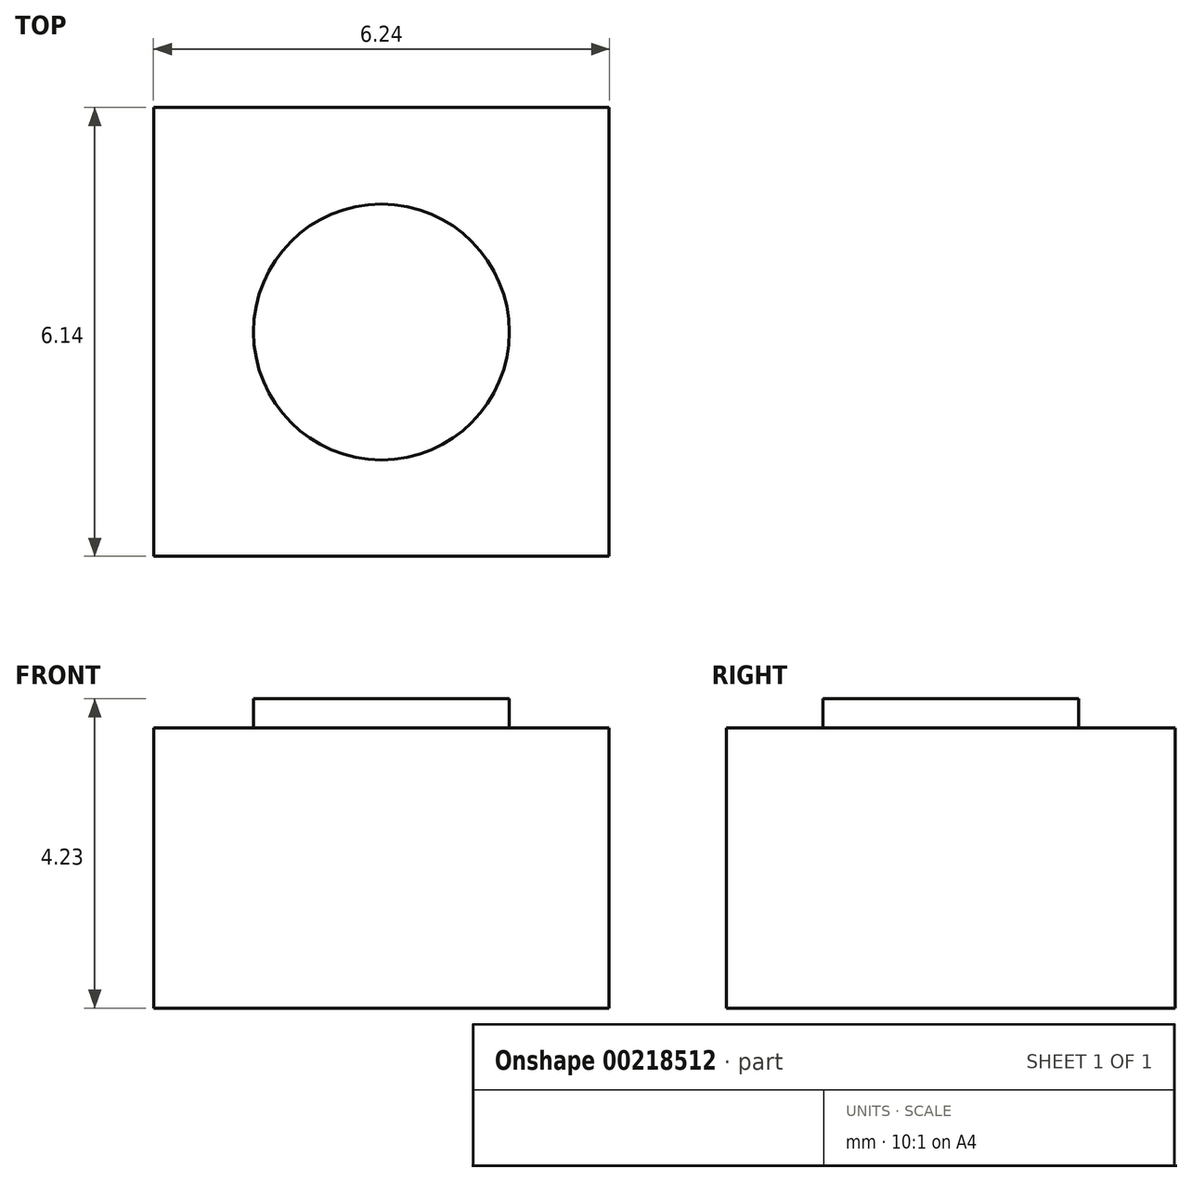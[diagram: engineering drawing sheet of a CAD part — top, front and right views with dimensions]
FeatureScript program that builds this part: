
annotation { "Feature Type Name" : "Feature", "Feature Type Description" : "" }
export const myFeature = defineFeature(function(context is Context, id is Id, definition is map)
    precondition{}
    {
        {
            var Q0;
            Q0=qCreatedBy(makeId("Top.planeOp"),FACE);
            var sketch = newSketch(context, id + "F0", { "sketchPlane" : qUnion([Q0])});
            skLineSegment(sketch, "E0.bottom", {"start": v(-3.12, 3.07) * mm, "end": v(3.12, 3.07) * mm});
            skLineSegment(sketch, "E0.top", {"start": v(-3.11, -3.07) * mm, "end": v(3.11, -3.07) * mm});
            skLineSegment(sketch, "E0.left", {"start": v(-3.11, 3.07) * mm, "end": v(-3.11, -3.07) * mm});
            skLineSegment(sketch, "E0.right", {"start": v(3.11, 3.07) * mm, "end": v(3.11, -3.07) * mm});
            skPoint(sketch, "E1", {"position": v(0, 3.07) * mm});
            skPoint(sketch, "E2", {"position": v(-3.11, 0) * mm});
            skSolve(sketch);
        }
        {
            var Q0;
            Q0 = qSketchRegion(id + "F0", true);
            var Q1;
            Q1=makeQuery(id+"F0.imprint","IMPRINT",FACE,{"disambiguationData":[TD([[makeQuery(id+"F0.imprint","IMPRINT",EDGE,{"derivedFrom":sQuery(id+"F0.wireOp",EDGE,"E0.bottom")}),-1.0]])]});
            extrude(context, id + "F1", {"entities" : qUnion([Q0, Q1]), "depth" : 3.83 * mm});
        }
        {
            var Q0;
            Q0=makeQuery(id+"F1.opExtrude","CAP_FACE",FACE,{"disambiguationData":[OSD([sQuery(id+"F0.wireOp",EDGE,"E0.bottom"),sQuery(id+"F0.wireOp",EDGE,"E0.top"),sQuery(id+"F0.wireOp",EDGE,"E0.left"),sQuery(id+"F0.wireOp",EDGE,"E0.right")])],"isStart":false});
            var sketch = newSketch(context, id + "F2", { "sketchPlane" : qUnion([Q0])});
            skCircle(sketch, "E3", {"center": v(0, 0) * mm, "radius": 1.75 * mm});
            skSolve(sketch);
        }
        {
            var Q0;
            Q0=makeQuery(id+"F2.imprint","IMPRINT",FACE,{"disambiguationData":[TD([[makeQuery(id+"F2.imprint","IMPRINT",EDGE,{"derivedFrom":sQuery(id+"F2.wireOp",EDGE,"E3")}),1.0]])]});
            extrude(context, id + "F3", {"entities" : qUnion([Q0]), "operationType" : NewBodyOperationType.ADD, "depth" : (4.23 - 3.83) * mm});
        }
    });
